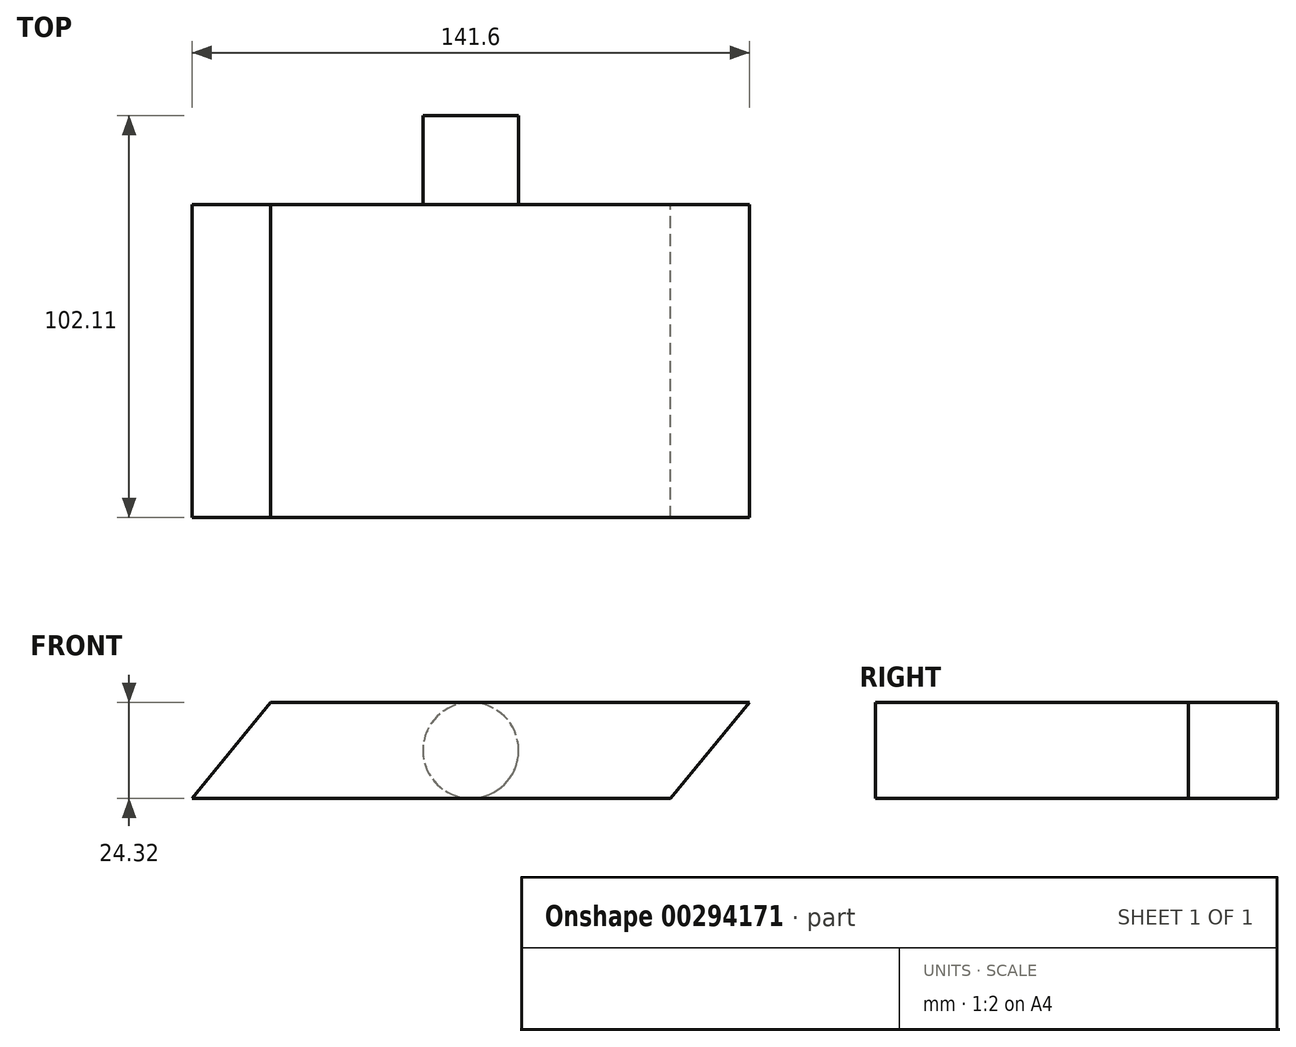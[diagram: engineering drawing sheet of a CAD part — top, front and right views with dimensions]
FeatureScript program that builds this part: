
annotation { "Feature Type Name" : "Feature", "Feature Type Description" : "" }
export const myFeature = defineFeature(function(context is Context, id is Id, definition is map)
    precondition{}
    {
        {
            var Q0;
            Q0=qCreatedBy(makeId("Front.planeOp"),FACE);
            var sketch = newSketch(context, id + "F0", { "sketchPlane" : qUnion([Q0])});
            skCircle(sketch, "E0", {"center": v(0, 0) * mm, "radius": 12.16 * mm});
            skSolve(sketch);
        }
        {
            var Q0;
            Q0 = qSketchRegion(id + "F0", true);
            extrude(context, id + "F1", {"entities" : qUnion([Q0]), "depth" : 22.6 * mm});
        }
        {
            var Q0;
            Q0=makeQuery(id+"F1.opExtrude","CAP_FACE",FACE,{"disambiguationData":[OSD([sQuery(id+"F0.wireOp",EDGE,"E0")])],"isStart":false});
            var sketch = newSketch(context, id + "F2", { "sketchPlane" : qUnion([Q0])});
            skLineSegment(sketch, "E1", {"start": v(0, 12.16) * mm, "end": v(50.8, 12.16) * mm});
            skLineSegment(sketch, "E2", {"start": v(0, 12.16) * mm, "end": v(-50.8, 12.16) * mm});
            skLineSegment(sketch, "E3", {"start": v(0, -12.16) * mm, "end": v(50.8, -12.16) * mm});
            skLineSegment(sketch, "E4", {"start": v(0, -12.16) * mm, "end": v(-50.8, -12.16) * mm});
            skLineSegment(sketch, "E5", {"start": v(-50.8, -12.16) * mm, "end": v(-70.8, -12.16) * mm});
            skLineSegment(sketch, "E6", {"start": v(-70.8, -12.16) * mm, "end": v(-50.8, 12.16) * mm});
            skLineSegment(sketch, "E7", {"start": v(50.8, 12.16) * mm, "end": v(70.8, 12.16) * mm});
            skLineSegment(sketch, "E8", {"start": v(70.8, 12.16) * mm, "end": v(50.8, -12.16) * mm});
            skSolve(sketch);
        }
        {
            var Q0;
            Q0 = qSketchRegion(id + "F2", true);
            extrude(context, id + "F3", {"entities" : qUnion([Q0]), "operationType" : NewBodyOperationType.ADD, "depth" : 79.5 * mm});
        }
    });
